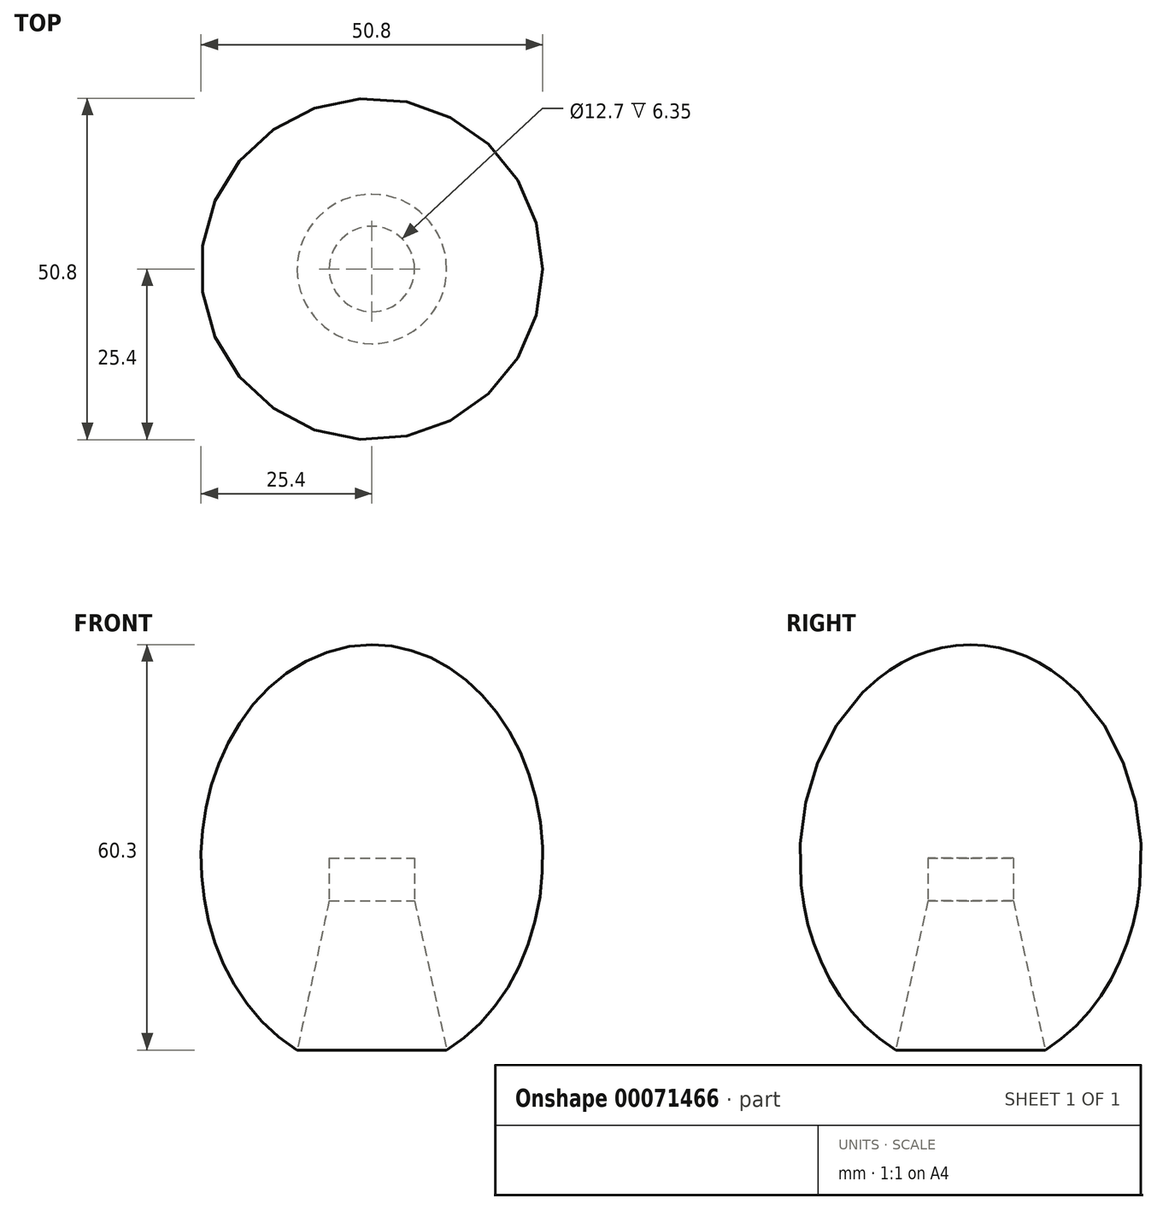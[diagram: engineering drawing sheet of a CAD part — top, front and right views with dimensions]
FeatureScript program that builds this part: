
annotation { "Feature Type Name" : "Feature", "Feature Type Description" : "" }
export const myFeature = defineFeature(function(context is Context, id is Id, definition is map)
    precondition{}
    {
        {
            var Q0;
            Q0=qCreatedBy(makeId("Front.planeOp"),FACE);
            var sketch = newSketch(context, id + "F0", { "sketchPlane" : qUnion([Q0])});
            skEllipticalArc(sketch, "E0", {});
            skLineSegment(sketch, "E1", {"start": v(0, 0) * mm, "end": v(6.35, 0) * mm});
            skLineSegment(sketch, "E2", {"start": v(6.35, 0) * mm, "end": v(6.35, -6.35) * mm});
            skLineSegment(sketch, "E3", {"start": v(0, -28.55) * mm, "end": v(11.11, -28.55) * mm});
            skLineSegment(sketch, "E4", {"start": v(6.35, -6.35) * mm, "end": v(11.11, -28.55) * mm});
            skLineSegment(sketch, "E5", {"start": v(0, 0) * mm, "end": v(0, 31.75) * mm});
            skPoint(sketch, "E6.end.orphan", {"position": v(0, -6.35) * mm});
            const initialGuessF0  = {"E0": [0, 0, 0, 1, 0.03175, 0.0254, 3.5944092483347174, 0]};
            skSetInitialGuess(sketch, initialGuessF0);
            skSolve(sketch);
        }
        {
            var Q0;
            Q0=makeQuery(id+"F0.imprint","IMPRINT",FACE,{"disambiguationData":[TD([[makeQuery(id+"F0.imprint","IMPRINT",EDGE,{"derivedFrom":sQuery(id+"F0.wireOp",EDGE,"E0")}),1.0]])]});
            var Q1;
            Q1=sQuery(id+"F0.wireOp",EDGE,"E5");
            revolve(context, id + "F1", {"entities" : qUnion([Q0]), "axis" : qUnion([Q1]), "revolveType" : RevolveType.FULL});
        }
    });
